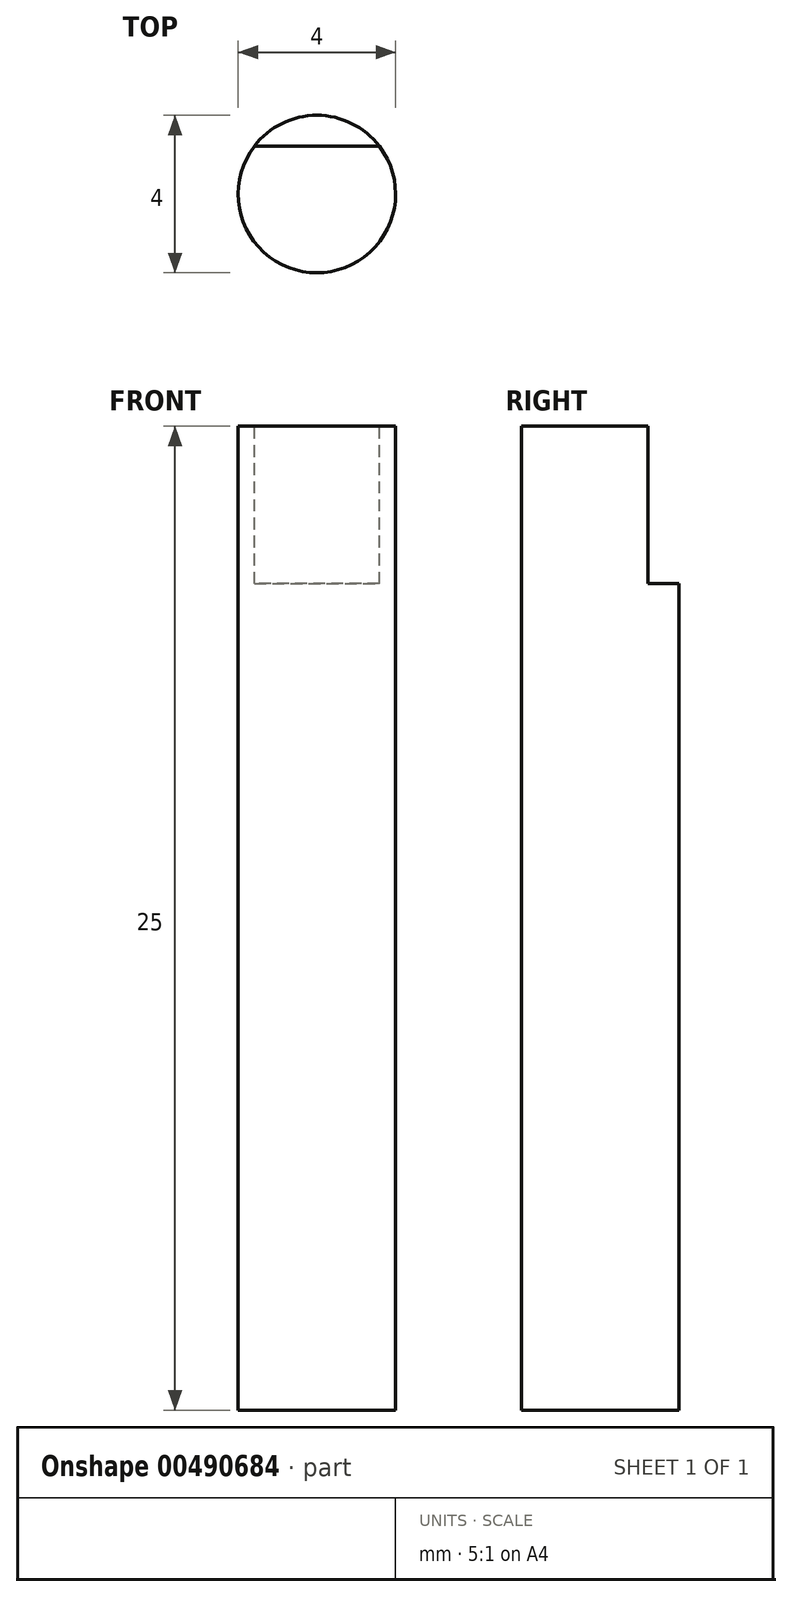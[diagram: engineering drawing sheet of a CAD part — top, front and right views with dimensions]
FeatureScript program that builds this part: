
annotation { "Feature Type Name" : "Feature", "Feature Type Description" : "" }
export const myFeature = defineFeature(function(context is Context, id is Id, definition is map)
    precondition{}
    {
        {
            var Q0;
            Q0=qCreatedBy(makeId("Top.planeOp"),FACE);
            var sketch = newSketch(context, id + "F0", { "sketchPlane" : qUnion([Q0])});
            skCircle(sketch, "E0", {"center": v(0, 0) * mm, "radius": 2 * mm});
            skSolve(sketch);
        }
        {
            var Q0;
            Q0=makeQuery(id+"F0.imprint","IMPRINT",FACE,{"disambiguationData":[TD([[makeQuery(id+"F0.imprint","IMPRINT",EDGE,{"derivedFrom":sQuery(id+"F0.wireOp",EDGE,"E0")}),1.0]])]});
            extrude(context, id + "F1", {"entities" : qUnion([Q0]), "depth" : 25 * mm, "offsetDistance" : 25 * mm});
        }
        {
            var Q0;
            Q0=makeQuery(id+"F1.opExtrude","CAP_FACE",FACE,{"disambiguationData":[OSD([sQuery(id+"F0.wireOp",EDGE,"E0")])],"isStart":false});
            var sketch = newSketch(context, id + "F2", { "sketchPlane" : qUnion([Q0])});
            skLineSegment(sketch, "E1", {"start": v(-1.59, 1.21) * mm, "end": v(1.59, 1.21) * mm});
            skSolve(sketch);
        }
        {
            var Q0;
            {var subQ0=sQuery(id+"F2.wireOp",EDGE,"E1");Q0=makeQuery(id+"F2.imprint","IMPRINT",FACE,{"disambiguationData":[TD([[makeQuery(id+"F2.imprint","IMPRINT",EDGE,{"derivedFrom":subQ0}),1.0]])]});}
            extrude(context, id + "F3", {"entities" : qUnion([Q0]), "operationType" : NewBodyOperationType.REMOVE, "oppositeDirection" : true, "depth" : 4 * mm, "offsetDistance" : 25 * mm});
        }
    });
